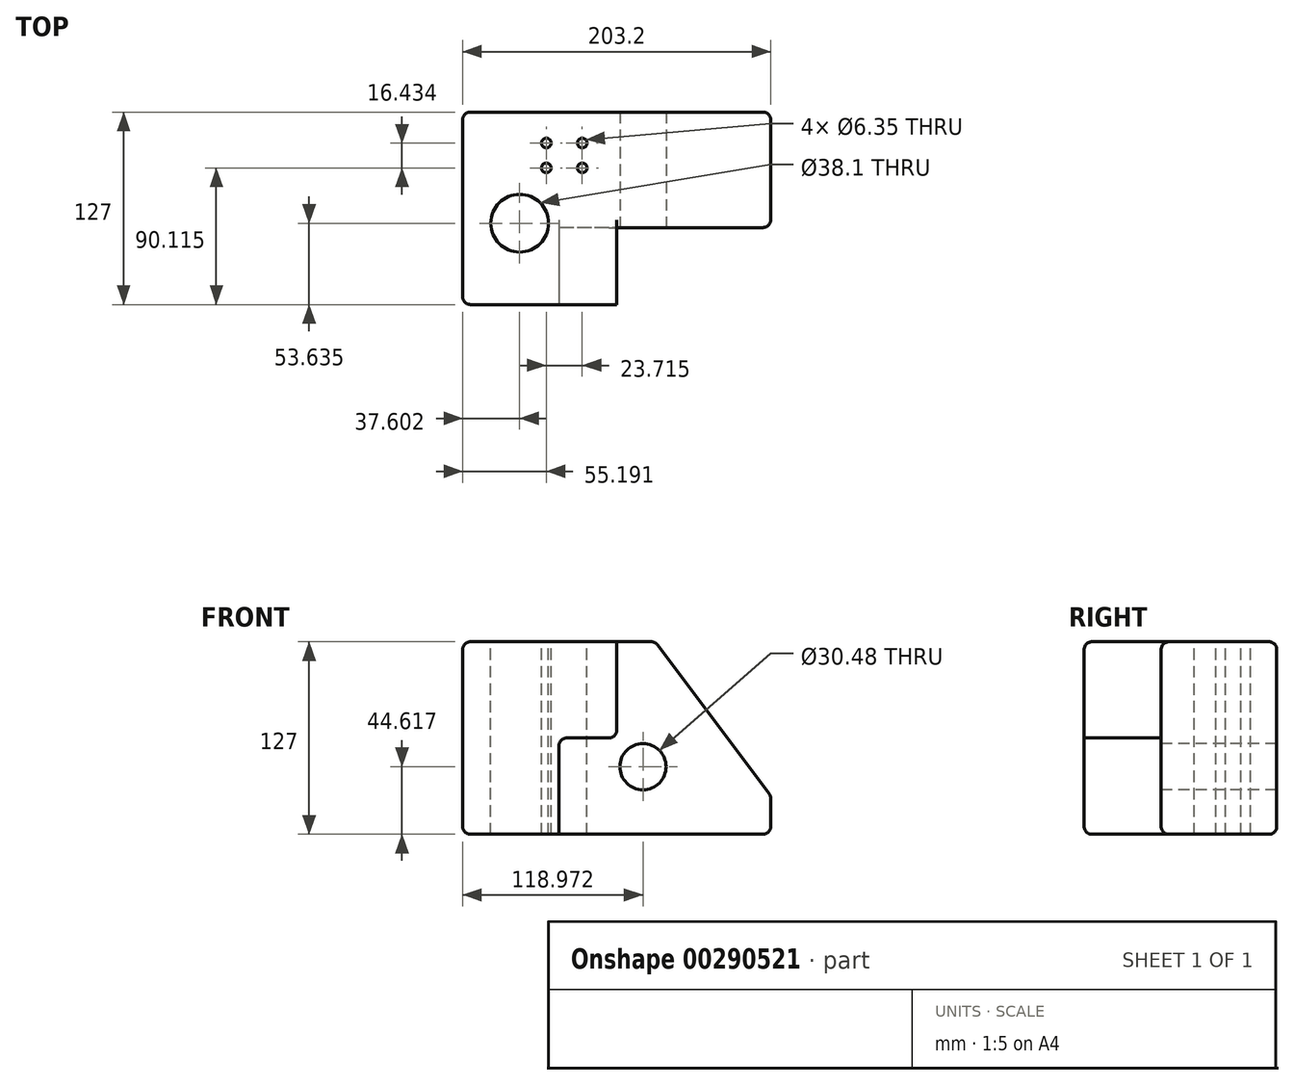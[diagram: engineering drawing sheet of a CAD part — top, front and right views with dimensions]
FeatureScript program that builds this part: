
annotation { "Feature Type Name" : "Feature", "Feature Type Description" : "" }
export const myFeature = defineFeature(function(context is Context, id is Id, definition is map)
    precondition{}
    {
        {
            var Q0;
            Q0=qCreatedBy(makeId("Front.planeOp"),FACE);
            var sketch = newSketch(context, id + "F0", { "sketchPlane" : qUnion([Q0])});
            skLineSegment(sketch, "E0.bottom", {"start": v(103.94, -63.5) * mm, "end": v(-99.26, -63.5) * mm});
            skLineSegment(sketch, "E0.top", {"start": v(103.94, 63.5) * mm, "end": v(-99.26, 63.5) * mm});
            skLineSegment(sketch, "E0.left", {"start": v(103.94, -63.5) * mm, "end": v(103.94, 63.5) * mm});
            skLineSegment(sketch, "E0.right", {"start": v(-99.26, -63.5) * mm, "end": v(-99.26, 63.5) * mm});
            skPoint(sketch, "E0.middle", {"position": v(2.34, 0) * mm});
            skSolve(sketch);
        }
        {
            var Q0;
            Q0 = qSketchRegion(id + "F0", true);
            extrude(context, id + "F1", {"entities" : qUnion([Q0]), "depth" : 127 * mm});
        }
        {
            var Q0;
            Q0=makeQuery(id+"F1.opExtrude","CAP_FACE",FACE,{"disambiguationData":[OSD([sQuery(id+"F0.wireOp",EDGE,"E0.bottom"),sQuery(id+"F0.wireOp",EDGE,"E0.top"),sQuery(id+"F0.wireOp",EDGE,"E0.left"),sQuery(id+"F0.wireOp",EDGE,"E0.right")])],"isStart":false});
            var sketch = newSketch(context, id + "F2", { "sketchPlane" : qUnion([Q0])});
            skLineSegment(sketch, "E1", {"start": v(-99.26, -63.5) * mm, "end": v(-99.26, 0) * mm});
            skLineSegment(sketch, "E2", {"start": v(-99.26, 0) * mm, "end": v(-99.26, 63.5) * mm});
            skLineSegment(sketch, "E3", {"start": v(-99.26, 63.5) * mm, "end": v(2.34, 63.5) * mm});
            skLineSegment(sketch, "E4", {"start": v(2.34, 63.5) * mm, "end": v(2.34, 0) * mm});
            skLineSegment(sketch, "E5", {"start": v(2.34, 0) * mm, "end": v(-35.76, 0) * mm});
            skLineSegment(sketch, "E6", {"start": v(-35.76, 0) * mm, "end": v(-35.76, -63.5) * mm});
            skLineSegment(sketch, "E7", {"start": v(-35.76, -63.5) * mm, "end": v(-99.26, -63.5) * mm});
            skSolve(sketch);
        }
        {
            var Q0;
            {var subQ3=sQuery(id+"F2.wireOp",EDGE,"E4");Q0=makeQuery(id+"F2.imprint","IMPRINT",FACE,{"disambiguationData":[TD([[makeQuery(id+"F2.imprint","IMPRINT",EDGE,{"derivedFrom":subQ3}),1.0]])]});}
            extrude(context, id + "F3", {"entities" : qUnion([Q0]), "operationType" : NewBodyOperationType.REMOVE, "oppositeDirection" : true, "depth" : 101.6 * mm});
        }
        {
            var Q0;
            Q0=makeQuery(id+"F3.boolean.opBoolean","COPY",FACE,{"derivedFrom":makeQuery(id+"F3.opExtrude","CAP_FACE",FACE,{"disambiguationData":[OSD([sQuery(id+"F0.wireOp",EDGE,"E0.bottom"),sQuery(id+"F0.wireOp",EDGE,"E0.top"),sQuery(id+"F0.wireOp",EDGE,"E0.left"),sQuery(id+"F2.wireOp",EDGE,"E4"),sQuery(id+"F2.wireOp",EDGE,"E5"),sQuery(id+"F2.wireOp",EDGE,"E6")])],"isStart":false})});
            extrude(context, id + "F4", {"entities" : qUnion([Q0]), "operationType" : NewBodyOperationType.ADD, "depth" : 50.8 * mm});
        }
        {
            var Q0;
            {var subQ0=sQuery(id+"F0.wireOp",EDGE,"E0.left");var subQ1=sQuery(id+"F0.wireOp",EDGE,"E0.top");Q0=makeQuery(id+"F4.boolean.opBoolean","MERGE",EDGE,{"derivedFrom":[makeQuery(id+"F1.opExtrude","SWEPT_EDGE",EDGE,{"disambiguationData":[OSD([subQ1,subQ0])]}),makeQuery(id+"F4.opExtrude","SWEPT_EDGE",EDGE,{"disambiguationData":[OSD([subQ1,subQ0])]})]});}
            chamfer(context, id + "F5", {"entities" : qUnion([Q0]), "chamferType" : ChamferType.TWO_OFFSETS, "width1" : 76.2 * mm, "oppositeDirection" : false, "width2" : 101.6 * mm, "tangentPropagation" : true});
        }
        {
            var Q0;
            Q0=makeQuery(id+"F1.opExtrude","CAP_EDGE",EDGE,{"disambiguationData":[OSD([sQuery(id+"F0.wireOp",EDGE,"E0.bottom")])],"isStart":false});
            var Q1;
            Q1=makeQuery(id+"F3.boolean.opBoolean","COPY",EDGE,{"derivedFrom":makeQuery(id+"F3.opExtrude","SWEPT_EDGE",EDGE,{"disambiguationData":[OSD([sQuery(id+"F2.wireOp",EDGE,"E4"),sQuery(id+"F2.wireOp",EDGE,"E5")])]})});
            var Q2;
            Q2=makeQuery(id+"F3.boolean.opBoolean","COPY",EDGE,{"derivedFrom":makeQuery(id+"F3.opExtrude","SWEPT_EDGE",EDGE,{"disambiguationData":[OSD([sQuery(id+"F0.wireOp",EDGE,"E0.bottom"),sQuery(id+"F2.wireOp",EDGE,"E6"),sQuery(id+"F2.wireOp",EDGE,"E7")])]})});
            var Q3;
            Q3=makeQuery(id+"F1.opExtrude","SWEPT_EDGE",EDGE,{"disambiguationData":[OSD([sQuery(id+"F0.wireOp",EDGE,"E0.top"),sQuery(id+"F0.wireOp",EDGE,"E0.right")])]});
            var Q4;
            Q4=makeQuery(id+"F3.boolean.opBoolean","COPY",EDGE,{"derivedFrom":makeQuery(id+"F3.opExtrude","SWEPT_EDGE",EDGE,{"disambiguationData":[OSD([sQuery(id+"F0.wireOp",EDGE,"E0.top"),sQuery(id+"F2.wireOp",EDGE,"E3"),sQuery(id+"F2.wireOp",EDGE,"E4")])]})});
            var Q5;
            Q5=makeQuery(id+"F4.opExtrude","CAP_EDGE",EDGE,{"disambiguationData":[OSD([sQuery(id+"F0.wireOp",EDGE,"E0.top")])],"isStart":false});
            var Q6;
            {var subQ0=sQuery(id+"F0.wireOp",EDGE,"E0.left");var subQ1=sQuery(id+"F0.wireOp",EDGE,"E0.top");Q6=makeQuery(id+"F5.opChamfer","BLEND_EDGE",EDGE,{"blendedFrom":[makeQuery(id+"F4.boolean.opBoolean","MERGE",EDGE,{"derivedFrom":[makeQuery(id+"F1.opExtrude","SWEPT_EDGE",EDGE,{"disambiguationData":[OSD([subQ1,subQ0])]}),makeQuery(id+"F4.opExtrude","SWEPT_EDGE",EDGE,{"disambiguationData":[OSD([subQ1,subQ0])]})]}),makeQuery(id+"F4.opExtrude","CAP_FACE",FACE,{"disambiguationData":[OSD([sQuery(id+"F0.wireOp",EDGE,"E0.bottom"),subQ1,subQ0,sQuery(id+"F2.wireOp",EDGE,"E4"),sQuery(id+"F2.wireOp",EDGE,"E5"),sQuery(id+"F2.wireOp",EDGE,"E6")])],"isStart":false})],"blendedInto":[makeQuery(id+"F4.opExtrude","CAP_FACE",FACE,{"disambiguationData":[OSD([sQuery(id+"F0.wireOp",EDGE,"E0.bottom"),subQ1,subQ0,sQuery(id+"F2.wireOp",EDGE,"E4"),sQuery(id+"F2.wireOp",EDGE,"E5"),sQuery(id+"F2.wireOp",EDGE,"E6")])],"isStart":false})]});}
            var Q7;
            Q7=makeQuery(id+"F3.boolean.opBoolean","COPY",EDGE,{"derivedFrom":makeQuery(id+"F3.opExtrude","CAP_EDGE",EDGE,{"disambiguationData":[OSD([sQuery(id+"F2.wireOp",EDGE,"E5")])],"isStart":true})});
            var Q8;
            {var subQ0=sQuery(id+"F0.wireOp",EDGE,"E0.left");var subQ1=sQuery(id+"F0.wireOp",EDGE,"E0.bottom");Q8=makeQuery(id+"F4.boolean.opBoolean","MERGE",EDGE,{"derivedFrom":[makeQuery(id+"F1.opExtrude","SWEPT_EDGE",EDGE,{"disambiguationData":[OSD([subQ1,subQ0])]}),makeQuery(id+"F4.opExtrude","SWEPT_EDGE",EDGE,{"disambiguationData":[OSD([subQ1,subQ0])]})]});}
            var Q9;
            Q9=makeQuery(id+"F1.opExtrude","CAP_EDGE",EDGE,{"disambiguationData":[OSD([sQuery(id+"F0.wireOp",EDGE,"E0.top")])],"isStart":true});
            var Q10;
            {var subQ0=sQuery(id+"F0.wireOp",EDGE,"E0.left");var subQ1=sQuery(id+"F0.wireOp",EDGE,"E0.top");Q10=makeQuery(id+"F5.opChamfer","BLEND_EDGE",EDGE,{"blendedFrom":[makeQuery(id+"F4.boolean.opBoolean","MERGE",EDGE,{"derivedFrom":[makeQuery(id+"F1.opExtrude","SWEPT_EDGE",EDGE,{"disambiguationData":[OSD([subQ1,subQ0])]}),makeQuery(id+"F4.opExtrude","SWEPT_EDGE",EDGE,{"disambiguationData":[OSD([subQ1,subQ0])]})]}),makeQuery(id+"F1.opExtrude","CAP_FACE",FACE,{"disambiguationData":[OSD([sQuery(id+"F0.wireOp",EDGE,"E0.bottom"),subQ1,subQ0,sQuery(id+"F0.wireOp",EDGE,"E0.right")])],"isStart":true})],"blendedInto":[makeQuery(id+"F1.opExtrude","CAP_FACE",FACE,{"disambiguationData":[OSD([sQuery(id+"F0.wireOp",EDGE,"E0.bottom"),subQ1,subQ0,sQuery(id+"F0.wireOp",EDGE,"E0.right")])],"isStart":true})]});}
            var Q11;
            Q11=makeQuery(id+"F4.opExtrude","CAP_EDGE",EDGE,{"disambiguationData":[OSD([sQuery(id+"F0.wireOp",EDGE,"E0.bottom")])],"isStart":false});
            var Q12;
            Q12=makeQuery(id+"F1.opExtrude","CAP_EDGE",EDGE,{"disambiguationData":[OSD([sQuery(id+"F0.wireOp",EDGE,"E0.top")])],"isStart":false});
            var Q13;
            {var subQ0=sQuery(id+"F0.wireOp",EDGE,"E0.top");var subQ1=sQuery(id+"F0.wireOp",EDGE,"E0.left");Q13=makeQuery(id+"F5.opChamfer","BLEND_EDGE",EDGE,{"blendedFrom":[makeQuery(id+"F4.boolean.opBoolean","MERGE",EDGE,{"derivedFrom":[makeQuery(id+"F1.opExtrude","SWEPT_EDGE",EDGE,{"disambiguationData":[OSD([subQ0,subQ1])]}),makeQuery(id+"F4.opExtrude","SWEPT_EDGE",EDGE,{"disambiguationData":[OSD([subQ0,subQ1])]})]}),makeQuery(id+"F4.boolean.opBoolean","MERGE",FACE,{"derivedFrom":[makeQuery(id+"F1.opExtrude","SWEPT_FACE",FACE,{"disambiguationData":[OSD([subQ0])]}),makeQuery(id+"F4.opExtrude","SWEPT_FACE",FACE,{"disambiguationData":[OSD([subQ0])]})]})],"blendedInto":[makeQuery(id+"F4.boolean.opBoolean","MERGE",FACE,{"derivedFrom":[makeQuery(id+"F1.opExtrude","SWEPT_FACE",FACE,{"disambiguationData":[OSD([subQ0])]}),makeQuery(id+"F4.opExtrude","SWEPT_FACE",FACE,{"disambiguationData":[OSD([subQ0])]})]})]});}
            var Q14;
            {var subQ0=sQuery(id+"F0.wireOp",EDGE,"E0.left");var subQ1=sQuery(id+"F0.wireOp",EDGE,"E0.top");Q14=makeQuery(id+"F5.opChamfer","BLEND_EDGE",EDGE,{"blendedFrom":[makeQuery(id+"F4.boolean.opBoolean","MERGE",EDGE,{"derivedFrom":[makeQuery(id+"F1.opExtrude","SWEPT_EDGE",EDGE,{"disambiguationData":[OSD([subQ1,subQ0])]}),makeQuery(id+"F4.opExtrude","SWEPT_EDGE",EDGE,{"disambiguationData":[OSD([subQ1,subQ0])]})]}),makeQuery(id+"F4.boolean.opBoolean","MERGE",FACE,{"derivedFrom":[makeQuery(id+"F1.opExtrude","SWEPT_FACE",FACE,{"disambiguationData":[OSD([subQ0])]}),makeQuery(id+"F4.opExtrude","SWEPT_FACE",FACE,{"disambiguationData":[OSD([subQ0])]})]})],"blendedInto":[makeQuery(id+"F4.boolean.opBoolean","MERGE",FACE,{"derivedFrom":[makeQuery(id+"F1.opExtrude","SWEPT_FACE",FACE,{"disambiguationData":[OSD([subQ0])]}),makeQuery(id+"F4.opExtrude","SWEPT_FACE",FACE,{"disambiguationData":[OSD([subQ0])]})]})]});}
            var Q15;
            Q15=makeQuery(id+"F4.opExtrude","CAP_EDGE",EDGE,{"disambiguationData":[OSD([sQuery(id+"F2.wireOp",EDGE,"E6")])],"isStart":false});
            var Q16;
            Q16=makeQuery(id+"F1.opExtrude","CAP_EDGE",EDGE,{"disambiguationData":[OSD([sQuery(id+"F0.wireOp",EDGE,"E0.right")])],"isStart":true});
            var Q17;
            Q17=makeQuery(id+"F4.opExtrude","CAP_EDGE",EDGE,{"disambiguationData":[OSD([sQuery(id+"F2.wireOp",EDGE,"E5")])],"isStart":false});
            var Q18;
            Q18=makeQuery(id+"F1.opExtrude","CAP_EDGE",EDGE,{"disambiguationData":[OSD([sQuery(id+"F0.wireOp",EDGE,"E0.bottom")])],"isStart":true});
            var Q19;
            Q19=makeQuery(id+"F1.opExtrude","CAP_EDGE",EDGE,{"disambiguationData":[OSD([sQuery(id+"F0.wireOp",EDGE,"E0.right")])],"isStart":false});
            var Q20;
            Q20=makeQuery(id+"F1.opExtrude","SWEPT_EDGE",EDGE,{"disambiguationData":[OSD([sQuery(id+"F0.wireOp",EDGE,"E0.bottom"),sQuery(id+"F0.wireOp",EDGE,"E0.right")])]});
            var Q21;
            Q21=makeQuery(id+"F3.boolean.opBoolean","COPY",EDGE,{"derivedFrom":makeQuery(id+"F3.opExtrude","SWEPT_EDGE",EDGE,{"disambiguationData":[OSD([sQuery(id+"F2.wireOp",EDGE,"E5"),sQuery(id+"F2.wireOp",EDGE,"E6")])]})});
            var Q22;
            Q22=makeQuery(id+"F4.opExtrude","CAP_EDGE",EDGE,{"disambiguationData":[OSD([sQuery(id+"F2.wireOp",EDGE,"E4")])],"isStart":false});
            var Q23;
            Q23=makeQuery(id+"F3.boolean.opBoolean","COPY",EDGE,{"derivedFrom":makeQuery(id+"F3.opExtrude","CAP_EDGE",EDGE,{"disambiguationData":[OSD([sQuery(id+"F2.wireOp",EDGE,"E4")])],"isStart":true})});
            var Q24;
            Q24=makeQuery(id+"F3.boolean.opBoolean","COPY",EDGE,{"derivedFrom":makeQuery(id+"F3.opExtrude","CAP_EDGE",EDGE,{"disambiguationData":[OSD([sQuery(id+"F2.wireOp",EDGE,"E6")])],"isStart":true})});
            var Q25;
            Q25=makeQuery(id+"F1.opExtrude","CAP_EDGE",EDGE,{"disambiguationData":[OSD([sQuery(id+"F0.wireOp",EDGE,"E0.left")])],"isStart":true});
            var Q26;
            Q26=makeQuery(id+"F4.opExtrude","CAP_EDGE",EDGE,{"disambiguationData":[OSD([sQuery(id+"F0.wireOp",EDGE,"E0.left")])],"isStart":false});
            fillet(context, id + "F6", {"entities" : qUnion([Q0, Q1, Q2, Q3, Q4, Q5, Q6, Q7, Q8, Q9, Q10, Q11, Q12, Q13, Q14, Q15, Q16, Q17, Q18, Q19, Q20, Q21, Q22, Q23, Q24, Q25, Q26]), "radius" : 5.08 * mm, "tangentPropagation" : true, "allowEdgeOverflow" : false});
        }
        {
            var Q0;
            Q0=makeQuery(id+"F4.opExtrude","CAP_FACE",FACE,{"disambiguationData":[OSD([sQuery(id+"F0.wireOp",EDGE,"E0.bottom"),sQuery(id+"F0.wireOp",EDGE,"E0.top"),sQuery(id+"F0.wireOp",EDGE,"E0.left"),sQuery(id+"F2.wireOp",EDGE,"E4"),sQuery(id+"F2.wireOp",EDGE,"E5"),sQuery(id+"F2.wireOp",EDGE,"E6")])],"isStart":false});
            var sketch = newSketch(context, id + "F7", { "sketchPlane" : qUnion([Q0])});
            skCircle(sketch, "E8", {"center": v(19.71, -18.88) * mm, "radius": 15.24 * mm});
            skLineSegment(sketch, "E9", {"start": v(-30.68, -40.02) * mm, "end": v(20.12, -40.02) * mm});
            skLineSegment(sketch, "E10", {"start": v(20.12, -40.02) * mm, "end": v(19.71, -18.88) * mm});
            skLineSegment(sketch, "E11", {"start": v(19.71, -18.88) * mm, "end": v(77.82, -17.77) * mm});
            skLineSegment(sketch, "E12", {"start": v(77.82, -17.77) * mm, "end": v(76.36, 58.42) * mm});
            skLineSegment(sketch, "E13", {"start": v(76.36, 58.42) * mm, "end": v(7.42, 58.42) * mm});
            skSolve(sketch);
        }
        {
            var Q0;
            {var subQ0=sQuery(id+"F7.wireOp",EDGE,"E10");var subQ1=sQuery(id+"F7.wireOp",EDGE,"E8");var subQ2=makeQuery(id+"F7.imprint","INTERSECT",VERTEX,{"derivedFrom":[subQ1,subQ0]});Q0=makeQuery(id+"F7.imprint","IMPRINT",FACE,{"disambiguationData":[TD([[makeQuery(id+"F7.imprint","IMPRINT",EDGE,{"disambiguationData":[TD([[subQ2,1.0]])],"derivedFrom":subQ1}),1.0]])]});}
            var Q1;
            {var subQ0=sQuery(id+"F7.wireOp",EDGE,"E10");var subQ1=sQuery(id+"F7.wireOp",EDGE,"E8");var subQ2=makeQuery(id+"F7.imprint","INTERSECT",VERTEX,{"derivedFrom":[subQ1,subQ0]});Q1=makeQuery(id+"F7.imprint","IMPRINT",FACE,{"disambiguationData":[TD([[makeQuery(id+"F7.imprint","IMPRINT",EDGE,{"disambiguationData":[TD([[subQ2,-1.0]])],"derivedFrom":subQ1}),1.0]])]});}
            var Q2;
            Q2=makeQuery(id+"F1.opExtrude","CAP_FACE",FACE,{"disambiguationData":[OSD([sQuery(id+"F0.wireOp",EDGE,"E0.bottom"),sQuery(id+"F0.wireOp",EDGE,"E0.top"),sQuery(id+"F0.wireOp",EDGE,"E0.left"),sQuery(id+"F0.wireOp",EDGE,"E0.right")])],"isStart":true});
            extrude(context, id + "F8", {"entities" : qUnion([Q0, Q1]), "operationType" : NewBodyOperationType.REMOVE, "endBound" : BoundingType.UP_TO_SURFACE, "oppositeDirection" : true, "endBoundEntityFace" : qUnion([Q2]), "depth" : 25.4 * mm});
        }
        {
            var Q0;
            {var subQ0=sQuery(id+"F0.wireOp",EDGE,"E0.top");Q0=makeQuery(id+"F4.boolean.opBoolean","MERGE",FACE,{"derivedFrom":[makeQuery(id+"F1.opExtrude","SWEPT_FACE",FACE,{"disambiguationData":[OSD([subQ0])]}),makeQuery(id+"F4.opExtrude","SWEPT_FACE",FACE,{"disambiguationData":[OSD([subQ0])]})]});}
            var sketch = newSketch(context, id + "F9", { "sketchPlane" : qUnion([Q0])});
            skCircle(sketch, "E14", {"center": v(-61.66, -73.37) * mm, "radius": 19.05 * mm});
            skSolve(sketch);
        }
        {
            var Q0;
            Q0=makeQuery(id+"F9.imprint","IMPRINT",FACE,{"disambiguationData":[TD([[makeQuery(id+"F9.imprint","IMPRINT",EDGE,{"derivedFrom":sQuery(id+"F9.wireOp",EDGE,"E14")}),1.0]])]});
            var Q1;
            {var subQ0=sQuery(id+"F0.wireOp",EDGE,"E0.bottom");Q1=makeQuery(id+"F4.boolean.opBoolean","MERGE",FACE,{"derivedFrom":[makeQuery(id+"F1.opExtrude","SWEPT_FACE",FACE,{"disambiguationData":[OSD([subQ0])]}),makeQuery(id+"F4.opExtrude","SWEPT_FACE",FACE,{"disambiguationData":[OSD([subQ0])]})]});}
            extrude(context, id + "F10", {"entities" : qUnion([Q0]), "operationType" : NewBodyOperationType.REMOVE, "endBound" : BoundingType.UP_TO_SURFACE, "oppositeDirection" : true, "endBoundEntityFace" : qUnion([Q1]), "depth" : 25.4 * mm});
        }
        {
            var Q0;
            Q0=makeQuery(id+"F9.imprint","IMPRINT",FACE,{"disambiguationData":[TD([[makeQuery(id+"F9.imprint","IMPRINT",EDGE,{"derivedFrom":sQuery(id+"F9.wireOp",EDGE,"E14")}),-1.0]])]});
            var sketch = newSketch(context, id + "F11", { "sketchPlane" : qUnion([Q0])});
            skPoint(sketch, "E15", {"position": v(-44.07, -36.89) * mm});
            skPoint(sketch, "E16", {"position": v(-20.35, -36.89) * mm});
            skPoint(sketch, "E17", {"position": v(-20.35, -20.45) * mm});
            skPoint(sketch, "E18", {"position": v(-44.07, -20.45) * mm});
            skSolve(sketch);
        }
        {
            var Q0;
            Q0=sQuery(id+"F11.wireOp",VERTEX,"E18");
            var Q1;
            Q1=sQuery(id+"F11.wireOp",VERTEX,"E15");
            var Q2;
            Q2=sQuery(id+"F11.wireOp",VERTEX,"E17");
            var Q3;
            Q3=sQuery(id+"F11.wireOp",VERTEX,"E16");
            var Q4;
            Q4=makeQuery(id+"F1.opExtrude","SWEPT_BODY",BODY,{"disambiguationData":[OSD([sQuery(id+"F0.wireOp",EDGE,"E0.bottom"),sQuery(id+"F0.wireOp",EDGE,"E0.top"),sQuery(id+"F0.wireOp",EDGE,"E0.left"),sQuery(id+"F0.wireOp",EDGE,"E0.right")])]});
            hole(context, id + "F12", {"style" : HoleStyle.SIMPLE, "endStyle" : HoleEndStyle.THROUGH, "holeDiameter" : 6.35 * mm, "isTappedThrough" : true, "tappedDepth" : 12.7 * mm, "tapClearance" : 3, "locations" : qUnion([Q0, Q1, Q2, Q3]), "scope" : qUnion([Q4])});
        }
    });
